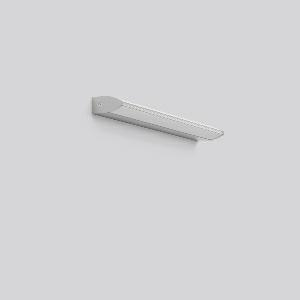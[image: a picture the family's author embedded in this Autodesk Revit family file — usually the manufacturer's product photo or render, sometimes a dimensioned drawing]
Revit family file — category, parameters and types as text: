
# Revit family: lavano_uno_451199_000_76_e5f3
name_source: partatom
category: Lighting Fixtures
units: mm (PartAtom-declared; Revit-internal decimal feet)

## family parameters
Cut with Voids When Loaded = No
Host = Face
Light Source = No
Part Type = Normal
Room Calculation Point = No
Round Connector Dimension = Use Diameter
Shared = No

## types (1)
- LAVANO UNO (1 x LED Modul 830, 2500 lm, 3000)
    Apparent Load = 19 VA
    CIE Flux Codes = 36 62 83 77 100
    Color Rendering = 80
    Color Temperature = 3000
    Default Elevation = 1800 mm
    Description = Series: LAVANO UNO
Linear LED surface-mounted luminaire in an elegant design. Extruded aluminium profile base, lacquered. End caps aluminium, painted. Diffuser: plastic, opal, allows for brilliant glittering light along the lines of the ellipse. Suitable for Ceiling mounting, Wall (surface). 
Colour: white aluminium (RAL 9006)
Length: 1140 mm
Width: 40 mm
Height: 83 mm
Lamp: LED
Socket: without socket
Colour temperature: 3000K
Colour rendering index (CRI): 80
System power: 19 W
Rated luminous flux: 2500 lm
Luminous efficiency: 132 lm/W
Control gear: Converter, dimmable, DALI
Protection class: I
Type of protection: IP 40
    Height = 83 mm
    Lamp = 1 x LED Modul 830
    Lamp Light Flux = 2500 lm
    Lamp count = 1
    Length = 1140 mm
    Lifetime = 50000 h
    Luminous efficacy = 132 lm/W
    Manufacturer = RZB
    ModVariant = No
    Model = 451199.000.76
    Mounting Place = Ceiling, Wall
    Mounting Type = Surface mounted
    Number of Poles = 1
    OnlyDefault = Yes
    Power Factor = 1
    Product Name = LAVANO UNO
    Product group = Surface mounted ceiling and wall luminaires
    ProductGroupID = 305
    Protection Class = Protection class I
    Protection Degree = IP 40
    RLX_Detail_Level = 1
    RLX_Emergency_Light_Flux = 0 lm
    RLX_Emergency_Type = 0
    RLX_Emergency_Type_DB = No
    RlxData = <blob elided: 24661 chars, md5=ccac0eae>
    Socket = socket
    Standby Power = 0 W
    System Light Flux = 2500 lm
    System Power = 19 W
    Type Comments = Product without accessories
    Type Image = 451100.000.jpg
    URL = http://relux.com
    VarID = ---
    Voltage = 230 V
    Voltage Range = 220-240 V
    Weight = 0.00 kg
    Width = 40 mm  [stored 0.131234 ft]

note: [stored X ft] marks values corroborated as IEEE doubles in the binary element streams (Revit-internal decimal feet)

## geometry (parser evidence)
native form markers: Blend x4, Sweep x12
no freeform markers — native parametric forms only
